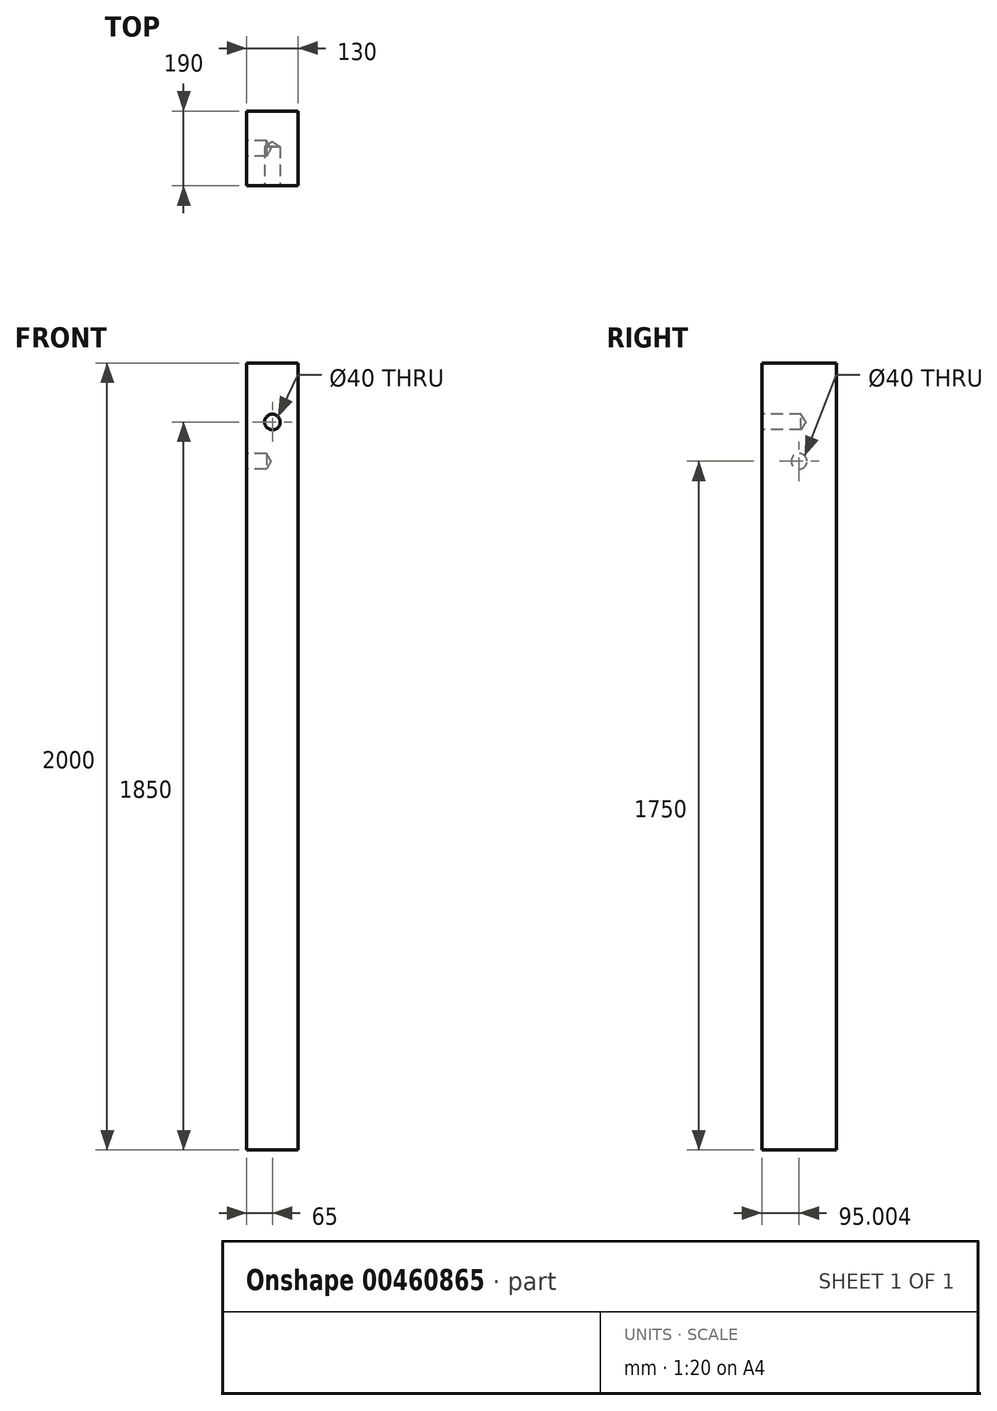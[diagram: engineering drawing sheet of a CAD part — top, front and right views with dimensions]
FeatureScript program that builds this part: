
annotation { "Feature Type Name" : "Feature", "Feature Type Description" : "" }
export const myFeature = defineFeature(function(context is Context, id is Id, definition is map)
    precondition{}
    {
        {
            var Q0;
            Q0=qCreatedBy(makeId("Top.planeOp"),FACE);
            var sketch = newSketch(context, id + "F0", { "sketchPlane" : qUnion([Q0])});
            skLineSegment(sketch, "E0.bottom", {"start": v(-65, 181.65) * mm, "end": v(65, 181.65) * mm});
            skLineSegment(sketch, "E0.top", {"start": v(-65, -8.35) * mm, "end": v(65, -8.35) * mm});
            skLineSegment(sketch, "E0.left", {"start": v(-65, 181.65) * mm, "end": v(-65, -8.35) * mm});
            skLineSegment(sketch, "E0.right", {"start": v(65, 181.65) * mm, "end": v(65, -8.35) * mm});
            skPoint(sketch, "E0.middle", {"position": v(0, 86.65) * mm});
            skLineSegment(sketch, "E1.bottom", {"start": v(34.26, 181.65) * mm, "end": v(-34.26, 181.65) * mm});
            skLineSegment(sketch, "E1.top", {"start": v(34.26, 181.65) * mm, "end": v(-34.26, 181.65) * mm});
            skLineSegment(sketch, "E1.left", {"start": v(34.26, 181.65) * mm, "end": v(34.26, 181.65) * mm});
            skLineSegment(sketch, "E1.right", {"start": v(-34.26, 181.65) * mm, "end": v(-34.26, 181.65) * mm});
            skPoint(sketch, "E1.middle", {"position": v(0, 181.65) * mm});
            skSolve(sketch);
        }
        {
            var Q0;
            Q0=makeQuery(id+"F0.imprint","IMPRINT",FACE,{"disambiguationData":[TD([[makeQuery(id+"F0.imprint","IMPRINT",EDGE,{"derivedFrom":sQuery(id+"F0.wireOp",EDGE,"E0.top")}),1.0]])]});
            extrude(context, id + "F1", {"entities" : qUnion([Q0]), "depth" : 2000 * mm});
        }
        {
            var Q0;
            Q0=makeQuery(id+"F1.opExtrude","SWEPT_FACE",FACE,{"disambiguationData":[OSD([sQuery(id+"F0.wireOp",EDGE,"E0.top")])]});
            var sketch = newSketch(context, id + "F2", { "sketchPlane" : qUnion([Q0])});
            skCircle(sketch, "E2", {"center": v(0, 1850) * mm, "radius": 20 * mm});
            skSolve(sketch);
        }
        {
            var Q0;
            Q0=sQuery(id+"F2.wireOp",VERTEX,"E2.center");
            var Q1;
            Q1=makeQuery(id+"F1.opExtrude","SWEPT_BODY",BODY,{"disambiguationData":[OSD([sQuery(id+"F0.wireOp",EDGE,"E0.bottom"),sQuery(id+"F0.wireOp",EDGE,"E0.top"),sQuery(id+"F0.wireOp",EDGE,"E0.left"),sQuery(id+"F0.wireOp",EDGE,"E0.right"),sQuery(id+"F0.wireOp",EDGE,"E1.top")])]});
            hole(context, id + "F3", {"style" : HoleStyle.SIMPLE, "endStyle" : HoleEndStyle.BLIND, "holeDiameter" : 40 * mm, "holeDepth" : 100 * mm, "isTappedThrough" : true, "tappedDepth" : 12 * mm, "tapClearance" : 3, "locations" : qUnion([Q0]), "scope" : qUnion([Q1])});
        }
        {
            var Q0;
            Q0=makeQuery(id+"F1.opExtrude","SWEPT_FACE",FACE,{"disambiguationData":[OSD([sQuery(id+"F0.wireOp",EDGE,"E0.left")])]});
            var sketch = newSketch(context, id + "F4", { "sketchPlane" : qUnion([Q0])});
            skCircle(sketch, "E3", {"center": v(-86.65, 1750) * mm, "radius": 20 * mm});
            skSolve(sketch);
        }
        {
            var Q0;
            Q0=sQuery(id+"F4.wireOp",VERTEX,"E3.center");
            var Q1;
            Q1=makeQuery(id+"F1.opExtrude","SWEPT_BODY",BODY,{"disambiguationData":[OSD([sQuery(id+"F0.wireOp",EDGE,"E0.bottom"),sQuery(id+"F0.wireOp",EDGE,"E0.top"),sQuery(id+"F0.wireOp",EDGE,"E0.left"),sQuery(id+"F0.wireOp",EDGE,"E0.right"),sQuery(id+"F0.wireOp",EDGE,"E1.top")])]});
            hole(context, id + "F5", {"style" : HoleStyle.SIMPLE, "endStyle" : HoleEndStyle.BLIND, "holeDiameter" : 40 * mm, "holeDepth" : 50 * mm, "isTappedThrough" : true, "tappedDepth" : 12 * mm, "tapClearance" : 3, "locations" : qUnion([Q0]), "scope" : qUnion([Q1])});
        }
    });
